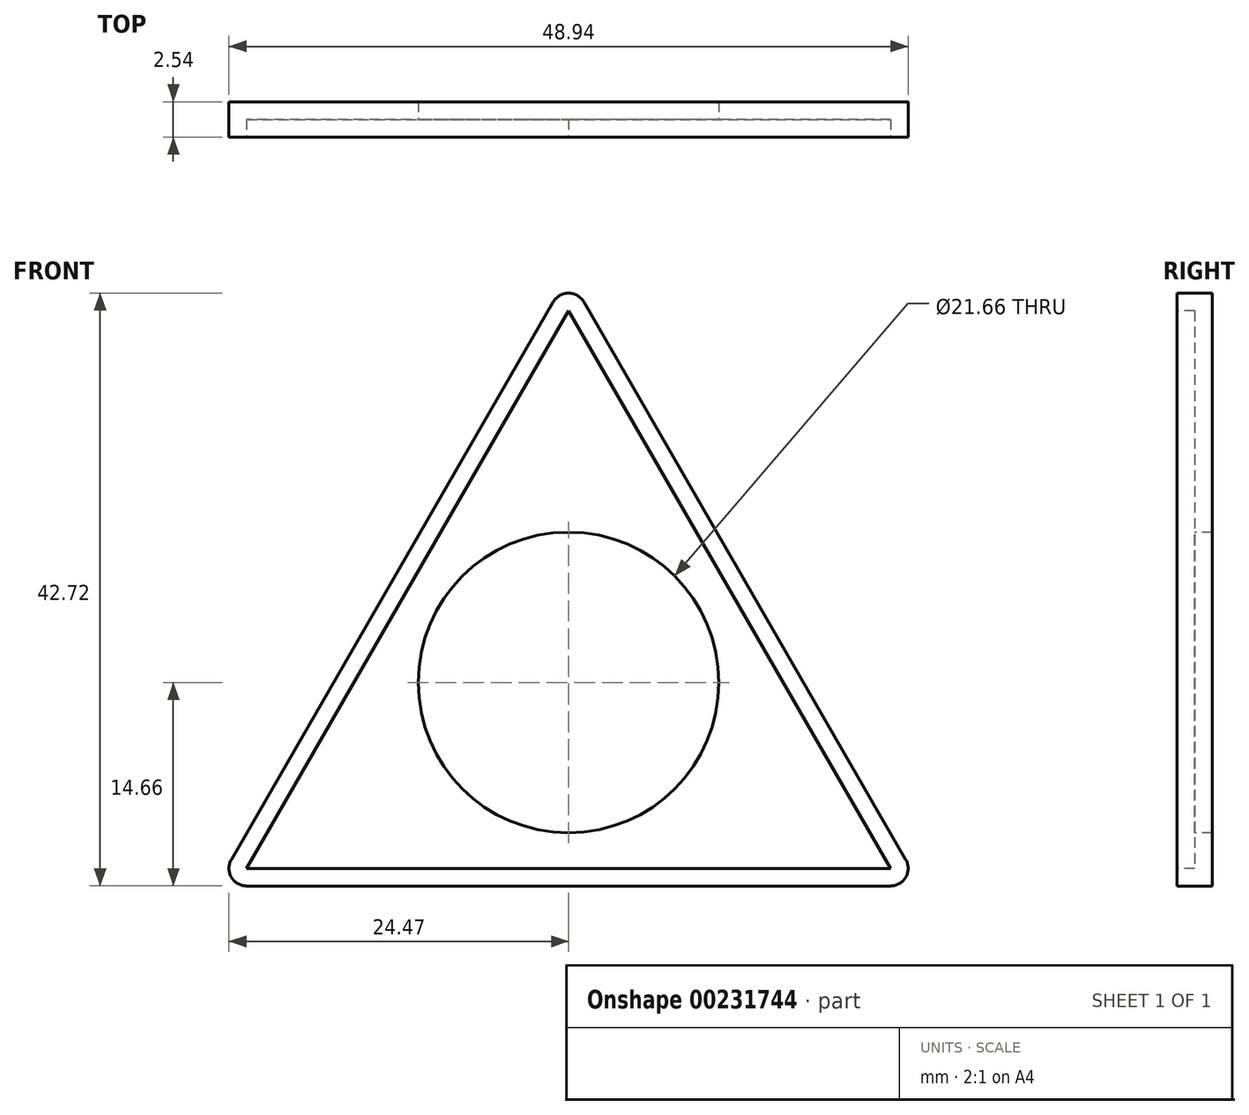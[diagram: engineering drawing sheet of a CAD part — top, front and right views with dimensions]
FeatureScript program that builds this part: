
annotation { "Feature Type Name" : "Feature", "Feature Type Description" : "" }
export const myFeature = defineFeature(function(context is Context, id is Id, definition is map)
    precondition{}
    {
        {
            var Q0;
            Q0=qCreatedBy(makeId("Front.planeOp"),FACE);
            var sketch = newSketch(context, id + "F0", { "sketchPlane" : qUnion([Q0])});
            skCircle(sketch, "E0.cCircle", {"center": v(0, 0) * mm, "radius": 14.66 * mm, "construction": true});
            skLineSegment(sketch, "E0.0", {"start": v(0, 29.33) * mm, "end": v(25.4, -14.66) * mm});
            skLineSegment(sketch, "E0.1", {"start": v(25.4, -14.66) * mm, "end": v(-25.4, -14.66) * mm});
            skLineSegment(sketch, "E0.2", {"start": v(-25.4, -14.66) * mm, "end": v(0, 29.33) * mm});
            skPoint(sketch, "E0.0.midPoint", {"position": v(12.7, 7.33) * mm});
            skSolve(sketch);
        }
        {
            var Q0;
            Q0=qSketchRegion(id+"F0",true);
            extrude(context, id + "F1", {"entities" : qUnion([Q0]), "depth" : 2.54 * mm});
        }
        {
            var Q0;
            Q0=makeQuery(id+"F1.opExtrude","SWEPT_EDGE",EDGE,{"disambiguationData":[OSD([sQuery(id+"F0.wireOp",EDGE,"E0.1"),sQuery(id+"F0.wireOp",EDGE,"E0.2")])]});
            var Q1;
            Q1=makeQuery(id+"F1.opExtrude","SWEPT_EDGE",EDGE,{"disambiguationData":[OSD([sQuery(id+"F0.wireOp",EDGE,"E0.0"),sQuery(id+"F0.wireOp",EDGE,"E0.1")])]});
            var Q2;
            Q2=makeQuery(id+"F1.opExtrude","SWEPT_EDGE",EDGE,{"disambiguationData":[OSD([sQuery(id+"F0.wireOp",EDGE,"E0.0"),sQuery(id+"F0.wireOp",EDGE,"E0.2")])]});
            fillet(context, id + "F2", {"entities" : qUnion([Q0, Q1, Q2]), "radius" : 1.27 * mm, "tangentPropagation" : true, "allowEdgeOverflow" : false});
        }
        {
            var Q0;
            Q0=makeQuery(id+"F1.opExtrude","CAP_FACE",FACE,{"disambiguationData":[OSD([sQuery(id+"F0.wireOp",EDGE,"E0.0"),sQuery(id+"F0.wireOp",EDGE,"E0.1"),sQuery(id+"F0.wireOp",EDGE,"E0.2")])],"isStart":false});
            shell(context, id + "F3", {"entities" : qUnion([Q0]), "thickness" : 1.27 * mm});
        }
        {
            var Q0;
            Q0=makeQuery(id+"F3.opShell","OFFSET_FACE",FACE,{"disambiguationData":[OSD([sQuery(id+"F0.wireOp",EDGE,"E0.0"),sQuery(id+"F0.wireOp",EDGE,"E0.1"),sQuery(id+"F0.wireOp",EDGE,"E0.2")])]});
            var sketch = newSketch(context, id + "F4", { "sketchPlane" : qUnion([Q0])});
            skCircle(sketch, "E1", {"center": v(0, 0) * mm, "radius": 10.83 * mm});
            skSolve(sketch);
        }
        {
            var Q0;
            Q0=qSketchRegion(id+"F4",true);
            extrude(context, id + "F5", {"entities" : qUnion([Q0]), "operationType" : NewBodyOperationType.REMOVE, "endBound" : BoundingType.THROUGH_ALL, "oppositeDirection" : true, "depth" : 25.4 * mm});
        }
    });
